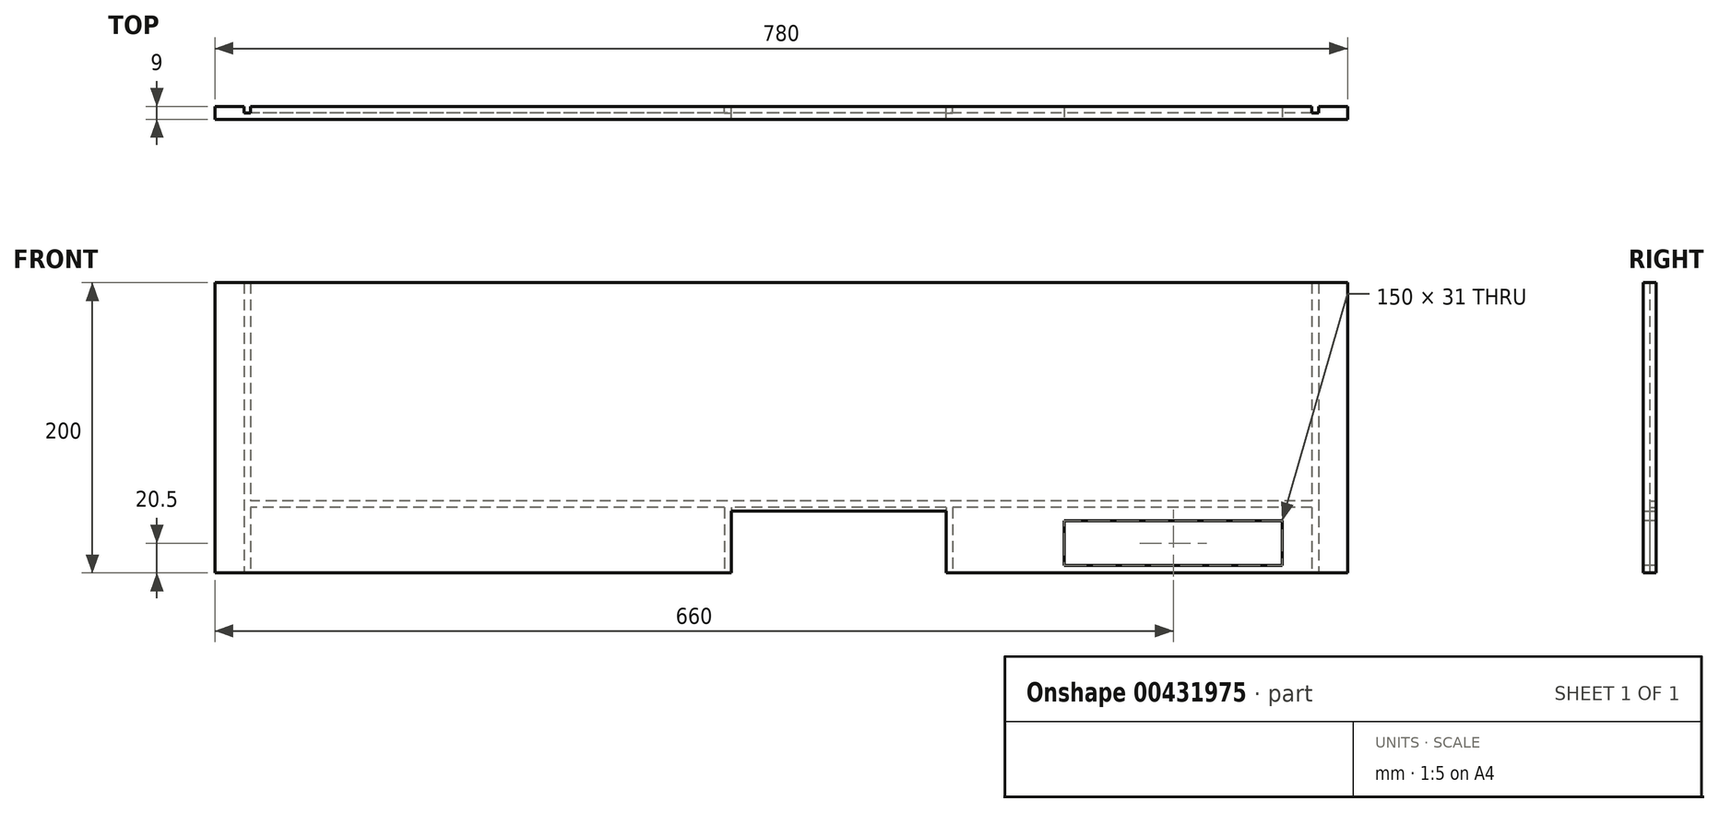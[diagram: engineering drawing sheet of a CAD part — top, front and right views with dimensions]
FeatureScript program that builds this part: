
annotation { "Feature Type Name" : "Feature", "Feature Type Description" : "" }
export const myFeature = defineFeature(function(context is Context, id is Id, definition is map)
    precondition{}
    {
        {
            var Q0;
            Q0=qCreatedBy(makeId("Front.planeOp"),FACE);
            var sketch = newSketch(context, id + "F0", { "sketchPlane" : qUnion([Q0])});
            skLineSegment(sketch, "E0.bottom", {"start": v(-370, 100) * mm, "end": v(370, 100) * mm});
            skLineSegment(sketch, "E0.top", {"start": v(-370, -100) * mm, "end": v(370, -100) * mm});
            skLineSegment(sketch, "E0.left", {"start": v(-370, 100) * mm, "end": v(-370, -100) * mm});
            skLineSegment(sketch, "E0.right", {"start": v(370, 100) * mm, "end": v(370, -100) * mm});
            skPoint(sketch, "E0.middle", {"position": v(0, 0) * mm});
            skSolve(sketch);
        }
        {
            var Q0;
            Q0=makeQuery(id+"F0.imprint","IMPRINT",FACE,{"disambiguationData":[TD([[makeQuery(id+"F0.imprint","IMPRINT",EDGE,{"derivedFrom":sQuery(id+"F0.wireOp",EDGE,"E0.bottom")}),-1.0]])]});
            extrude(context, id + "F1", {"entities" : qUnion([Q0]), "depth" : 9 * mm, "offsetDistance" : 25 * mm});
        }
        {
            var Q0;
            Q0=makeQuery(id+"F1.opExtrude","SWEPT_FACE",FACE,{"disambiguationData":[OSD([sQuery(id+"F0.wireOp",EDGE,"E0.right")])]});
            var sketch = newSketch(context, id + "F2", { "sketchPlane" : qUnion([Q0])});
            skLineSegment(sketch, "E1.bottom", {"start": v(0, 100) * mm, "end": v(-4.5, 100) * mm});
            skLineSegment(sketch, "E1.top", {"start": v(0, -100) * mm, "end": v(-4.5, -100) * mm});
            skLineSegment(sketch, "E1.left", {"start": v(0, 100) * mm, "end": v(0, -100) * mm});
            skLineSegment(sketch, "E1.right", {"start": v(-4.5, 100) * mm, "end": v(-4.5, -100) * mm});
            skSolve(sketch);
        }
        {
            var Q0;
            Q0=qSketchRegion(id+"F2",true);
            extrude(context, id + "F3", {"entities" : qUnion([Q0]), "operationType" : NewBodyOperationType.REMOVE, "oppositeDirection" : true, "depth" : 4.5 * mm, "offsetDistance" : 25 * mm});
        }
        {
            var Q0;
            Q0=makeQuery(id+"F1.opExtrude","SWEPT_FACE",FACE,{"disambiguationData":[OSD([sQuery(id+"F0.wireOp",EDGE,"E0.left")])]});
            var sketch = newSketch(context, id + "F4", { "sketchPlane" : qUnion([Q0])});
            skLineSegment(sketch, "E2.bottom", {"start": v(0, 100) * mm, "end": v(4.5, 100) * mm});
            skLineSegment(sketch, "E2.top", {"start": v(0, -100) * mm, "end": v(4.5, -100) * mm});
            skLineSegment(sketch, "E2.left", {"start": v(0, 100) * mm, "end": v(0, -100) * mm});
            skLineSegment(sketch, "E2.right", {"start": v(4.5, 100) * mm, "end": v(4.5, -100) * mm});
            skSolve(sketch);
        }
        {
            var Q0;
            Q0=qSketchRegion(id+"F4",true);
            extrude(context, id + "F5", {"entities" : qUnion([Q0]), "operationType" : NewBodyOperationType.REMOVE, "oppositeDirection" : true, "depth" : 4.5 * mm, "offsetDistance" : 25 * mm});
        }
        {
            var Q0;
            Q0=makeQuery(id+"F1.opExtrude","CAP_FACE",FACE,{"disambiguationData":[OSD([sQuery(id+"F0.wireOp",EDGE,"E0.bottom"),sQuery(id+"F0.wireOp",EDGE,"E0.top"),sQuery(id+"F0.wireOp",EDGE,"E0.left"),sQuery(id+"F0.wireOp",EDGE,"E0.right")])],"isStart":true});
            var sketch = newSketch(context, id + "F6", { "sketchPlane" : qUnion([Q0])});
            skLineSegment(sketch, "E3.bottom", {"start": v(-365.5, -50.5) * mm, "end": v(365.5, -50.5) * mm});
            skLineSegment(sketch, "E3.top", {"start": v(-365.5, -55) * mm, "end": v(365.5, -55) * mm});
            skLineSegment(sketch, "E3.left", {"start": v(-365.5, -50.5) * mm, "end": v(-365.5, -55) * mm});
            skLineSegment(sketch, "E3.right", {"start": v(365.5, -50.5) * mm, "end": v(365.5, -55) * mm});
            skSolve(sketch);
        }
        {
            var Q0;
            Q0=qSketchRegion(id+"F6",true);
            extrude(context, id + "F7", {"entities" : qUnion([Q0]), "operationType" : NewBodyOperationType.REMOVE, "oppositeDirection" : true, "depth" : 4.5 * mm, "offsetDistance" : 25 * mm});
        }
        {
            var Q0;
            Q0=makeQuery(id+"F1.opExtrude","CAP_FACE",FACE,{"disambiguationData":[OSD([sQuery(id+"F0.wireOp",EDGE,"E0.bottom"),sQuery(id+"F0.wireOp",EDGE,"E0.top"),sQuery(id+"F0.wireOp",EDGE,"E0.left"),sQuery(id+"F0.wireOp",EDGE,"E0.right")])],"isStart":false});
            var sketch = newSketch(context, id + "F8", { "sketchPlane" : qUnion([Q0])});
            skLineSegment(sketch, "E4.bottom", {"start": v(345, -95) * mm, "end": v(195, -95) * mm});
            skLineSegment(sketch, "E4.top", {"start": v(345, -64) * mm, "end": v(195, -64) * mm});
            skLineSegment(sketch, "E4.left", {"start": v(345, -95) * mm, "end": v(345, -64) * mm});
            skLineSegment(sketch, "E4.right", {"start": v(195, -95) * mm, "end": v(195, -64) * mm});
            skPoint(sketch, "E4.middle", {"position": v(270, -79.5) * mm});
            skSolve(sketch);
        }
        {
            var Q0;
            Q0=qSketchRegion(id+"F8",true);
            extrude(context, id + "F9", {"entities" : qUnion([Q0]), "operationType" : NewBodyOperationType.REMOVE, "endBound" : BoundingType.UP_TO_NEXT, "oppositeDirection" : true, "depth" : 25 * mm});
        }
        {
            var Q0;
            {var subQ0=sQuery(id+"F0.wireOp",EDGE,"E0.top");Q0=makeQuery(id+"F7.boolean.opBoolean","SPLIT",FACE,{"disambiguationData":[TD([makeQuery(id+"F1.opExtrude","SWEPT_FACE",FACE,{"disambiguationData":[OSD([subQ0])]})])],"derivedFrom":makeQuery(id+"F1.opExtrude","CAP_FACE",FACE,{"disambiguationData":[OSD([sQuery(id+"F0.wireOp",EDGE,"E0.bottom"),subQ0,sQuery(id+"F0.wireOp",EDGE,"E0.left"),sQuery(id+"F0.wireOp",EDGE,"E0.right")])],"isStart":true})});}
            var sketch = newSketch(context, id + "F10", { "sketchPlane" : qUnion([Q0])});
            skLineSegment(sketch, "E5.bottom", {"start": v(-113.5, -57.5) * mm, "end": v(34.5, -57.5) * mm});
            skLineSegment(sketch, "E5.top", {"start": v(-113.5, -100) * mm, "end": v(34.5, -100) * mm});
            skLineSegment(sketch, "E5.left", {"start": v(-113.5, -57.5) * mm, "end": v(-113.5, -100) * mm});
            skLineSegment(sketch, "E5.right", {"start": v(34.5, -57.5) * mm, "end": v(34.5, -100) * mm});
            skSolve(sketch);
        }
        {
            var Q0;
            Q0=qSketchRegion(id+"F10",true);
            extrude(context, id + "F11", {"entities" : qUnion([Q0]), "operationType" : NewBodyOperationType.REMOVE, "endBound" : BoundingType.THROUGH_ALL, "oppositeDirection" : true, "depth" : 25 * mm});
        }
        {
            var Q0;
            {var subQ0=sQuery(id+"F0.wireOp",EDGE,"E0.top");Q0=makeQuery(id+"F7.boolean.opBoolean","SPLIT",FACE,{"disambiguationData":[TD([makeQuery(id+"F1.opExtrude","SWEPT_FACE",FACE,{"disambiguationData":[OSD([subQ0])]})])],"derivedFrom":makeQuery(id+"F1.opExtrude","CAP_FACE",FACE,{"disambiguationData":[OSD([sQuery(id+"F0.wireOp",EDGE,"E0.bottom"),subQ0,sQuery(id+"F0.wireOp",EDGE,"E0.left"),sQuery(id+"F0.wireOp",EDGE,"E0.right")])],"isStart":true})});}
            var sketch = newSketch(context, id + "F12", { "sketchPlane" : qUnion([Q0])});
            skLineSegment(sketch, "E6.bottom", {"start": v(34.5, -55) * mm, "end": v(39, -55) * mm});
            skLineSegment(sketch, "E6.top", {"start": v(34.5, -100) * mm, "end": v(39, -100) * mm});
            skLineSegment(sketch, "E6.left", {"start": v(34.5, -55) * mm, "end": v(34.5, -100) * mm});
            skLineSegment(sketch, "E6.right", {"start": v(39, -55) * mm, "end": v(39, -100) * mm});
            skLineSegment(sketch, "E7.bottom", {"start": v(-113.5, -55) * mm, "end": v(-118, -55) * mm});
            skLineSegment(sketch, "E7.top", {"start": v(-113.5, -100) * mm, "end": v(-118, -100) * mm});
            skLineSegment(sketch, "E7.left", {"start": v(-113.5, -55) * mm, "end": v(-113.5, -100) * mm});
            skLineSegment(sketch, "E7.right", {"start": v(-118, -55) * mm, "end": v(-118, -100) * mm});
            skSolve(sketch);
        }
        {
            var Q0;
            Q0=qSketchRegion(id+"F12",true);
            extrude(context, id + "F13", {"entities" : qUnion([Q0]), "operationType" : NewBodyOperationType.REMOVE, "oppositeDirection" : true, "depth" : 4.5 * mm, "offsetDistance" : 25 * mm});
        }
        {
            var Q0;
            Q0=makeQuery(id+"F1.opExtrude","SWEPT_FACE",FACE,{"disambiguationData":[OSD([sQuery(id+"F0.wireOp",EDGE,"E0.right")])]});
            var sketch = newSketch(context, id + "F14", { "sketchPlane" : qUnion([Q0])});
            skLineSegment(sketch, "E8.bottom", {"start": v(-9, 100) * mm, "end": v(0, 100) * mm});
            skLineSegment(sketch, "E8.top", {"start": v(-9, -100) * mm, "end": v(0, -100) * mm});
            skLineSegment(sketch, "E8.left", {"start": v(-9, 100) * mm, "end": v(-9, -100) * mm});
            skLineSegment(sketch, "E8.right", {"start": v(0, 100) * mm, "end": v(0, -100) * mm});
            skSolve(sketch);
        }
        {
            var Q0;
            Q0=qSketchRegion(id+"F14",true);
            extrude(context, id + "F15", {"entities" : qUnion([Q0]), "operationType" : NewBodyOperationType.ADD, "depth" : 20 * mm});
        }
        {
            var Q0;
            Q0=makeQuery(id+"F1.opExtrude","SWEPT_FACE",FACE,{"disambiguationData":[OSD([sQuery(id+"F0.wireOp",EDGE,"E0.left")])]});
            var sketch = newSketch(context, id + "F16", { "sketchPlane" : qUnion([Q0])});
            skLineSegment(sketch, "E9.bottom", {"start": v(9, 100) * mm, "end": v(0, 100) * mm});
            skLineSegment(sketch, "E9.top", {"start": v(9, -100) * mm, "end": v(0, -100) * mm});
            skLineSegment(sketch, "E9.left", {"start": v(9, 100) * mm, "end": v(9, -100) * mm});
            skLineSegment(sketch, "E9.right", {"start": v(0, 100) * mm, "end": v(0, -100) * mm});
            skSolve(sketch);
        }
        {
            var Q0;
            Q0=qSketchRegion(id+"F16",true);
            extrude(context, id + "F17", {"entities" : qUnion([Q0]), "operationType" : NewBodyOperationType.ADD, "depth" : 20 * mm});
        }
    });
